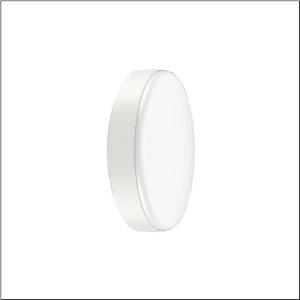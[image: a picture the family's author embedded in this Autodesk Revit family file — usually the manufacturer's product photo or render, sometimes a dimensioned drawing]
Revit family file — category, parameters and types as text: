
# Revit family: round_31_51wc10mb34a
name_source: partatom
category: Lighting Fixtures
units: mm (PartAtom-declared; Revit-internal decimal feet)

## family parameters
Cut with Voids When Loaded = No
Host = Face
Light Source = No
Part Type = Normal
Room Calculation Point = No
Round Connector Dimension = Use Diameter
Shared = No

## types (1)
- --- (1 x LED, 4250 lm, 34 W, 3000K)
    Apparent Load = 34 VA
    CIE Flux Codes = 44 75 94 94 100
    Color Rendering = 80
    Color Temperature = 3000K
    Default Elevation = 1800 mm
    Description = Round 31, wall and ceiling luminaire, primary optical cover: cover, of PC, opal, light emission: direct distribution, primary light characteristic: symmetric, installation type: surface-mounted, LED, rated luminous flux: 4.250lm, luminous efficacy: 125lm/W, light colour: 830, colour temperature: 3000K, control gear: ON/OFF Multilumen, with terminal, 3-pole, max. 2.5mm², mains connection: 220..240V, AC, 50/60Hz, rated input power: 34W, luminaire housing, of PC, traffic white (RAL 9016), diameter: 480mm, protection rating (complete): IP65, insulation class (complete): insulation class II (safety insulation), certification: CE, impact resistance: IK10, permissible operating ambient temperature: -20..+40°C, permissible storage temperature: -20..+60°C, packaging unit: 1 piece
    Height = 97 mm
    Lamp = 1 x LED
    Lamp Light Flux = 4250 lm
    Lamp Power = 34 W
    Lamp count = 1
    Length = 480 mm
    Luminous efficacy = 125 lm/W
    Manufacturer = Siteco
    ModVariant = No
    Model = 51WC10MB34A
    Mounting Place = Wall
    Mounting Type = Surface mounted
    Number of Poles = 1
    OnlyDefault = Yes
    Power Factor = 1
    Product Name = Round 31
    Product group = wall and ceiling luminaire | wall mounted
    ProductGroupID = 2001
    Protection Class = Protection class II
    Protection Degree = IP 65
    RLX_Detail_Level = 1
    RLX_Emergency_Light_Flux = 0 lm
    RLX_Emergency_Type = 0
    RLX_Emergency_Type_DB = No
    RlxData = <blob elided: 56429 chars, md5=c9f742d7>
    Socket = socket
    Standby Power = 0 W
    System Light Flux = 4250 lm
    System Power = 34 W
    Type Comments = factory setting: luminous flux: 100 % | (ON | ON)
    Type Image = l_1007188.jpg
    URL = http://relux.com
    VarID = @adj_151905
    Voltage = 0 V
    Weight = 0.00 kg
    Width = 0 mm  [stored 0 ft]

note: [stored X ft] marks values corroborated as IEEE doubles in the binary element streams (Revit-internal decimal feet)

## geometry (parser evidence)
native form markers: Blend x4, Sweep x12
no freeform markers — native parametric forms only
